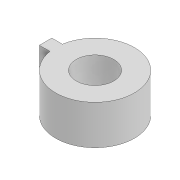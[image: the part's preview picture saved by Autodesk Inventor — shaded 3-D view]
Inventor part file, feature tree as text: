
AUTODESK INVENTOR PART (.ipt)
format: ipt  version: 2022 (Build 260153000, 153)  size: 91,136 bytes
history: native  units: mm
features: extrude x1, sketch x1
ambient origin geometry x8: Origin, YZ Plane, XZ Plane, XY Plane, X Axis, Y Axis, Z Axis, Center Point
bodies: Solid1 (feature_tree)
feature tree (2):
  extrude  "Extrusion1"  Depth=10.0mm
  sketch  "Sketch1"  dims[d0=20.0mm d1=9.534878mm d2=10.0mm d3=0.0mm]
